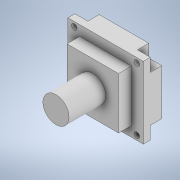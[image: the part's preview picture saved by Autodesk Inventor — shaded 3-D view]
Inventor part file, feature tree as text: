
AUTODESK INVENTOR PART (.ipt)
format: ipt  version: 2022.1 (Build 261234000, 234)  size: 155,136 bytes
history: native  units: in
note: dims shown in document units (in); Inventor stores cm internally (conversion verified against a paired STEP export)
features: extrude x4, sketch x4
ambient origin geometry x8: Origin, YZ Plane, XZ Plane, XY Plane, X Axis, Y Axis, Z Axis, Center Point
bodies: Solid1 (feature_tree)
feature tree (8):
  extrude  "Extrusion1"  Depth=1.5354in
  extrude  "Extrusion2"  Depth=1.3386in
  extrude  "Extrusion3"  Depth=0.3937in
  extrude  "Extrusion4"  Depth=1.1024in
  sketch  "Sketch1"  dims[d0=1.6142in d1=1.5354in]
  sketch  "Sketch2"  dims[d2=1.3386in d3=1.3386in]
  sketch  "Sketch3"  dims[d4=0.1181in d5=0.3937in]
  sketch  "Sketch4"  dims[d6=0.0in d7=1.1024in d8=1.1024in d9=0.2756in d10=0.0in d11=0.5591in d12=0.7874in d13=0.0in d14=0.2756in d15=0.2441in d16=0.0in]
